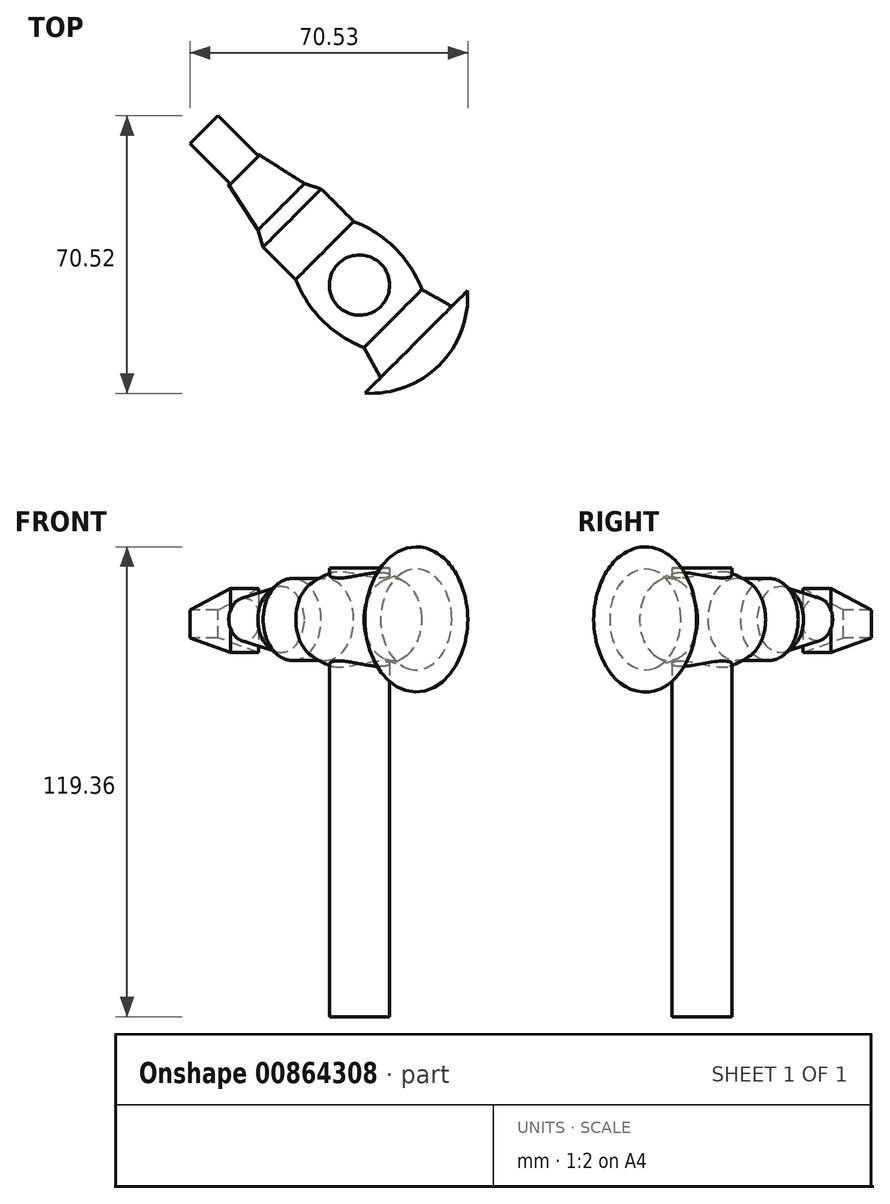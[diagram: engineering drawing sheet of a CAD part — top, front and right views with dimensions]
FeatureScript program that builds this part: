
annotation { "Feature Type Name" : "Feature", "Feature Type Description" : "" }
export const myFeature = defineFeature(function(context is Context, id is Id, definition is map)
    precondition{}
    {
        {
            var Q0;
            Q0=qCreatedBy(makeId("Top.planeOp"),FACE);
            cPlane(context, id + "F0", {"entities" : qUnion([Q0]), "cplaneType" : CPlaneType.OFFSET, "offset" : 36 * mm, "oppositeDirection" : true, "width" : 150 * mm, "height" : 150 * mm});
        }
        {
            var Q0;
            Q0=qCreatedBy(makeId("Top.planeOp"),FACE);
            cPlane(context, id + "F1", {"entities" : qUnion([Q0]), "cplaneType" : CPlaneType.OFFSET, "offset" : 40 * mm, "width" : 150 * mm, "height" : 150 * mm});
        }
        {
            var Q0;
            Q0=qCreatedBy(makeId("Front.planeOp"),FACE);
            var sketch = newSketch(context, id + "F2", { "sketchPlane" : qUnion([Q0])});
            skLineSegment(sketch, "E0", {"start": v(0, 86.74) * mm, "end": v(0, -86.44) * mm});
            skSolve(sketch);
        }
        {
            var Q0;
            Q0=sQuery(id+"F2.wireOp",EDGE,"E0");
            var Q1;
            Q1=qCreatedBy(makeId("Front.planeOp"),FACE);
            cPlane(context, id + "F3", {"entities" : qUnion([Q0, Q1]), "cplaneType" : CPlaneType.LINE_ANGLE, "offset" : 25 * mm, "angle" : 45 * degree, "width" : 150 * mm, "height" : 150 * mm});
        }
        {
            var Q0;
            Q0=qCreatedBy(id+"F3.planeOp",FACE);
            cPlane(context, id + "F4", {"entities" : qUnion([Q0]), "cplaneType" : CPlaneType.OFFSET, "offset" : 25 * mm, "width" : 150 * mm, "height" : 150 * mm});
        }
        {
            var Q0;
            Q0=qCreatedBy(id+"F4.planeOp",FACE);
            var sketch = newSketch(context, id + "F5", { "sketchPlane" : qUnion([Q0])});
            skLineSegment(sketch, "E1", {"start": v(-75.39, 49.92) * mm, "end": v(-11.92, 49.92) * mm});
            skLineSegment(sketch, "E2", {"start": v(-11.92, 49.92) * mm, "end": v(-11.92, 55.3) * mm});
            skLineSegment(sketch, "E3", {"start": v(-73.9, 62.7) * mm, "end": v(-73.9, 68.36) * mm});
            skLineSegment(sketch, "E4", {"start": v(-29.35, 60.33) * mm, "end": v(-41.03, 60.33) * mm});
            skArc(sketch, "E5", {"start": v(-41.03, 60.33) * mm, "mid": v(-53.27, 62.93) * mm, "end": v(-65.52, 60.33) * mm});
            skLineSegment(sketch, "E6", {"start": v(-65.52, 60.33) * mm, "end": v(-73.9, 62.7) * mm});
            skLineSegment(sketch, "E7", {"start": v(-11.92, 55.3) * mm, "end": v(-25.37, 58.26) * mm});
            skLineSegment(sketch, "E8", {"start": v(-25.37, 58.26) * mm, "end": v(-29.35, 60.33) * mm});
            skArc(sketch, "E9", {"start": v(-73.9, 68.36) * mm, "mid": v(-80.03, 60.03) * mm, "end": v(-82.2, 49.92) * mm});
            skLineSegment(sketch, "E10", {"start": v(-75.39, 49.92) * mm, "end": v(-82.2, 49.92) * mm});
            skSolve(sketch);
        }
        {
            var Q0;
            Q0=qSketchRegion(id+"F5",true);
            var Q1;
            Q1=sQuery(id+"F5.wireOp",EDGE,"E1");
            revolve(context, id + "F6", {"surfaceOperationType" : NewSurfaceOperationType.NEW, "entities" : qUnion([Q0]), "axis" : qUnion([Q1]), "revolveType" : RevolveType.FULL});
        }
        {
            var Q0;
            Q0=qCreatedBy(id+"F4.planeOp",FACE);
            var sketch = newSketch(context, id + "F7", { "sketchPlane" : qUnion([Q0])});
            skLineSegment(sketch, "E11", {"start": v(-12.2, 57.73) * mm, "end": v(-12.2, 41.5) * mm});
            skLineSegment(sketch, "E12", {"start": v(-12.2, 41.5) * mm, "end": v(2.33, 45.24) * mm});
            skLineSegment(sketch, "E13", {"start": v(2.33, 45.24) * mm, "end": v(2.33, 52.3) * mm});
            skLineSegment(sketch, "E14", {"start": v(2.33, 52.3) * mm, "end": v(-12.2, 57.73) * mm});
            skSolve(sketch);
        }
        {
            var Q0;
            Q0=qSketchRegion(id+"F7",true);
            extrude(context, id + "F8", {"entities" : qUnion([Q0]), "operationType" : NewBodyOperationType.ADD, "depth" : 5 * mm, "offsetDistance" : 25 * mm});
        }
        {
            var Q0;
            Q0=qSketchRegion(id+"F7",true);
            extrude(context, id + "F9", {"entities" : qUnion([Q0]), "operationType" : NewBodyOperationType.ADD, "oppositeDirection" : true, "depth" : 5 * mm, "offsetDistance" : 25 * mm});
        }
        {
            var Q0;
            Q0=qCreatedBy(id+"F0.planeOp",FACE);
            var sketch = newSketch(context, id + "F10", { "sketchPlane" : qUnion([Q0])});
            skCircle(sketch, "E15", {"center": v(55.51, -20.16) * mm, "radius": 7.65 * mm});
            skSolve(sketch);
        }
        {
            var Q0;
            Q0=qSketchRegion(id+"F10",true);
            extrude(context, id + "F11", {"entities" : qUnion([Q0]), "operationType" : NewBodyOperationType.ADD, "depth" : 99 * mm, "offsetDistance" : 25 * mm});
        }
        {
            var Q0;
            Q0=qSketchRegion(id+"F10",true);
            extrude(context, id + "F12", {"entities" : qUnion([Q0]), "operationType" : NewBodyOperationType.ADD, "oppositeDirection" : true, "depth" : 15 * mm, "offsetDistance" : 25 * mm});
        }
    });
